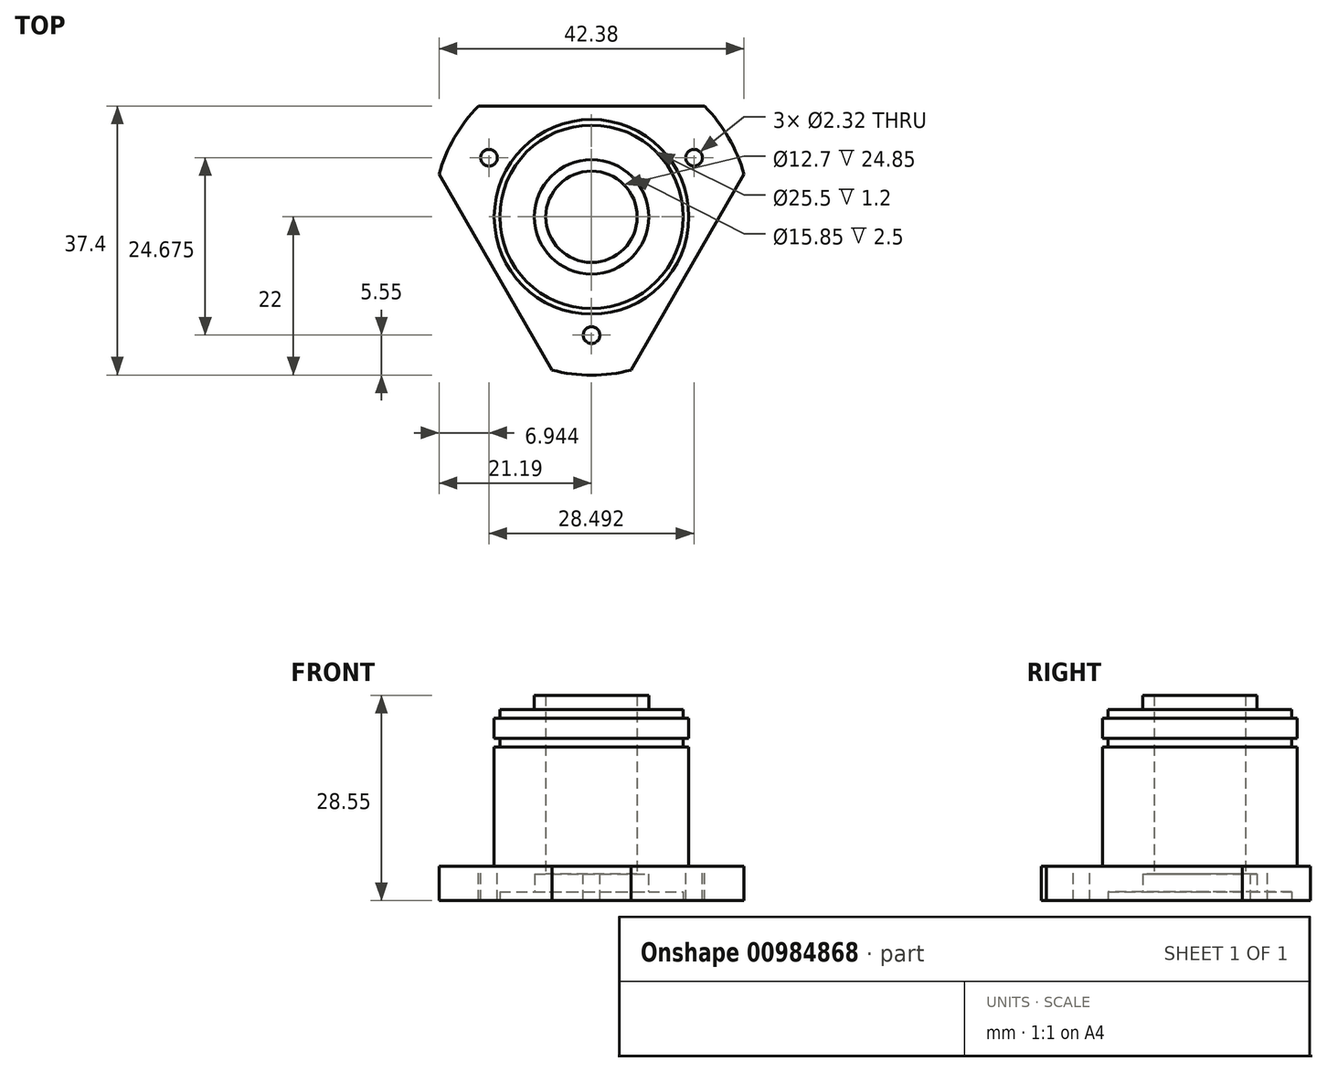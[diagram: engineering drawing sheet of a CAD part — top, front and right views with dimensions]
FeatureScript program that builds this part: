
annotation { "Feature Type Name" : "Feature", "Feature Type Description" : "" }
export const myFeature = defineFeature(function(context is Context, id is Id, definition is map)
    precondition{}
    {
        {
            var Q0;
            Q0=qCreatedBy(makeId("Top.planeOp"),FACE);
            var sketch = newSketch(context, id + "F0", { "sketchPlane" : qUnion([Q0])});
            skCircle(sketch, "E0", {"center": v(0, 0) * mm, "radius": 13.53 * mm});
            skCircle(sketch, "E1", {"center": v(0, 0) * mm, "radius": 6.35 * mm});
            skSolve(sketch);
        }
        {
            var Q0;
            Q0=makeQuery(id+"F0.imprint","IMPRINT",FACE,{"disambiguationData":[TD([[makeQuery(id+"F0.imprint","IMPRINT",EDGE,{"derivedFrom":sQuery(id+"F0.wireOp",EDGE,"E0")}),1.0]])]});
            extrude(context, id + "F1", {"entities" : qUnion([Q0]), "depth" : 23.8 * mm, "offsetDistance" : 25 * mm});
        }
        {
            var Q0;
            Q0=makeQuery(id+"F1.opExtrude","CAP_FACE",FACE,{"disambiguationData":[OSD([sQuery(id+"F0.wireOp",EDGE,"E0"),sQuery(id+"F0.wireOp",EDGE,"E1")])],"isStart":false});
            var sketch = newSketch(context, id + "F2", { "sketchPlane" : qUnion([Q0])});
            skCircle(sketch, "E2", {"center": v(0, 0) * mm, "radius": 13.53 * mm});
            skCircle(sketch, "E3", {"center": v(0, 0) * mm, "radius": 7.95 * mm});
            skSolve(sketch);
        }
        {
            var Q0;
            Q0=makeQuery(id+"F2.imprint","IMPRINT",FACE,{"disambiguationData":[TD([[makeQuery(id+"F2.imprint","IMPRINT",EDGE,{"derivedFrom":sQuery(id+"F2.wireOp",EDGE,"E2")}),1.0]])]});
            extrude(context, id + "F3", {"entities" : qUnion([Q0]), "operationType" : NewBodyOperationType.REMOVE, "oppositeDirection" : true, "depth" : 2 * mm, "offsetDistance" : 25 * mm});
        }
        {
            var Q0;
            Q0=makeQuery(id+"F3.boolean.opBoolean","COPY",FACE,{"derivedFrom":makeQuery(id+"F3.opExtrude","CAP_FACE",FACE,{"disambiguationData":[OSD([sQuery(id+"F2.wireOp",EDGE,"E2"),sQuery(id+"F2.wireOp",EDGE,"E3")])],"isStart":false})});
            var sketch = newSketch(context, id + "F4", { "sketchPlane" : qUnion([Q0])});
            skCircle(sketch, "E4", {"center": v(0, 0) * mm, "radius": 12.75 * mm});
            skCircle(sketch, "E5", {"center": v(0, 0) * mm, "radius": 13.53 * mm});
            skSolve(sketch);
        }
        {
            var Q0;
            Q0=makeQuery(id+"F4.imprint","IMPRINT",FACE,{"disambiguationData":[TD([[makeQuery(id+"F4.imprint","IMPRINT",EDGE,{"derivedFrom":sQuery(id+"F4.wireOp",EDGE,"E4")}),-1.0]])]});
            extrude(context, id + "F5", {"entities" : qUnion([Q0]), "operationType" : NewBodyOperationType.REMOVE, "oppositeDirection" : true, "depth" : 1.2 * mm, "offsetDistance" : 25 * mm});
        }
        {
            var Q0;
            Q0=makeQuery(id+"F1.opExtrude","CAP_FACE",FACE,{"disambiguationData":[OSD([sQuery(id+"F0.wireOp",EDGE,"E0"),sQuery(id+"F0.wireOp",EDGE,"E1")])],"isStart":true});
            var sketch = newSketch(context, id + "F6", { "sketchPlane" : qUnion([Q0])});
            skCircle(sketch, "E6", {"center": v(0, 0) * mm, "radius": 22 * mm});
            skCircle(sketch, "E7", {"center": v(0, 16.45) * mm, "radius": 1.16 * mm});
            skCircle(sketch, "E8.1.1", {"center": v(-14.25, -8.22) * mm, "radius": 1.16 * mm});
            skCircle(sketch, "E8.2.1", {"center": v(14.25, -8.23) * mm, "radius": 1.16 * mm});
            skLineSegment(sketch, "E9", {"start": v(-15.71, -15.4) * mm, "end": v(15.71, -15.4) * mm});
            skPoint(sketch, "E10", {"position": v(0, -15.4) * mm});
            skPoint(sketch, "E11.orphan", {"position": v(-16.5, -15.4) * mm});
            skPoint(sketch, "E12.orphan", {"position": v(16.5, -15.4) * mm});
            skLineSegment(sketch, "E13.1.0", {"start": v(21.2, -5.9) * mm, "end": v(5.48, 21.3) * mm});
            skLineSegment(sketch, "E13.2.0", {"start": v(-5.48, 21.3) * mm, "end": v(-21.2, -5.9) * mm});
            skSolve(sketch);
        }
        {
            var Q0;
            Q0=makeQuery(id+"F6.imprint","IMPRINT",FACE,{"disambiguationData":[TD([[makeQuery(id+"F6.imprint","IMPRINT",EDGE,{"derivedFrom":sQuery(id+"F6.wireOp",EDGE,"E7")}),-1.0]])]});
            var Q1;
            Q1=makeQuery(id+"F6.imprint","IMPRINT",FACE,{"disambiguationData":[TD([[makeQuery(id+"F6.imprint","IMPRINT",EDGE,{"derivedFrom":makeQuery(id+"F1.opExtrude","CAP_EDGE",EDGE,{"disambiguationData":[OSD([sQuery(id+"F0.wireOp",EDGE,"E0")])],"isStart":true})}),-1.0]])]});
            extrude(context, id + "F7", {"entities" : qUnion([Q0, Q1]), "operationType" : NewBodyOperationType.ADD, "depth" : 4.75 * mm, "offsetDistance" : 25 * mm});
        }
        {
            var Q0;
            Q0=makeQuery(id+"F7.opExtrude","CAP_FACE",FACE,{"disambiguationData":[OSD([sQuery(id+"F0.wireOp",EDGE,"E1"),sQuery(id+"F6.wireOp",EDGE,"E7"),sQuery(id+"F6.wireOp",EDGE,"E8.1.1"),sQuery(id+"F6.wireOp",EDGE,"E6"),sQuery(id+"F6.wireOp",EDGE,"E8.2.1"),sQuery(id+"F6.wireOp",EDGE,"E9"),sQuery(id+"F6.wireOp",EDGE,"E13.1.0"),sQuery(id+"F6.wireOp",EDGE,"E13.2.0")])],"isStart":false});
            var sketch = newSketch(context, id + "F8", { "sketchPlane" : qUnion([Q0])});
            skCircle(sketch, "E14", {"center": v(0, 0) * mm, "radius": 12.75 * mm});
            skSolve(sketch);
        }
        {
            var Q0;
            Q0=makeQuery(id+"F8.imprint","IMPRINT",FACE,{"disambiguationData":[TD([[makeQuery(id+"F8.imprint","IMPRINT",EDGE,{"derivedFrom":sQuery(id+"F8.wireOp",EDGE,"E14")}),1.0]])]});
            extrude(context, id + "F9", {"entities" : qUnion([Q0]), "operationType" : NewBodyOperationType.REMOVE, "oppositeDirection" : true, "depth" : 1.2 * mm, "offsetDistance" : 25 * mm});
        }
        {
            var Q0;
            Q0=makeQuery(id+"F9.boolean.opBoolean","COPY",FACE,{"derivedFrom":makeQuery(id+"F9.opExtrude","CAP_FACE",FACE,{"disambiguationData":[OSD([sQuery(id+"F0.wireOp",EDGE,"E1"),sQuery(id+"F8.wireOp",EDGE,"E14")])],"isStart":false})});
            var sketch = newSketch(context, id + "F10", { "sketchPlane" : qUnion([Q0])});
            skCircle(sketch, "E15", {"center": v(0, 0) * mm, "radius": 7.92 * mm});
            skSolve(sketch);
        }
        {
            var Q0;
            Q0=makeQuery(id+"F10.imprint","IMPRINT",FACE,{"disambiguationData":[TD([[makeQuery(id+"F10.imprint","IMPRINT",EDGE,{"derivedFrom":sQuery(id+"F10.wireOp",EDGE,"E15")}),1.0]])]});
            extrude(context, id + "F11", {"entities" : qUnion([Q0]), "operationType" : NewBodyOperationType.REMOVE, "oppositeDirection" : true, "depth" : 2.5 * mm, "offsetDistance" : 25 * mm});
        }
        {
            var Q0;
            Q0=makeQuery(id+"F3.boolean.opBoolean","COPY",FACE,{"derivedFrom":makeQuery(id+"F3.opExtrude","CAP_FACE",FACE,{"disambiguationData":[OSD([sQuery(id+"F2.wireOp",EDGE,"E2"),sQuery(id+"F2.wireOp",EDGE,"E3")])],"isStart":false})});
            cPlane(context, id + "F12", {"entities" : qUnion([Q0]), "cplaneType" : CPlaneType.OFFSET, "offset" : 4 * mm, "oppositeDirection" : true, "width" : 150 * mm, "height" : 150 * mm});
        }
        {
            var Q0;
            Q0=qCreatedBy(id+"F12.planeOp",FACE);
            var sketch = newSketch(context, id + "F13", { "sketchPlane" : qUnion([Q0])});
            skCircle(sketch, "E16", {"center": v(0, 0) * mm, "radius": 13.53 * mm});
            skCircle(sketch, "E17", {"center": v(0, 0) * mm, "radius": 12.75 * mm});
            skSolve(sketch);
        }
        {
            var Q0;
            Q0 = qSketchRegion(id + "F13", true);
            extrude(context, id + "F14", {"entities" : qUnion([Q0]), "operationType" : NewBodyOperationType.REMOVE, "oppositeDirection" : true, "depth" : 1.2 * mm, "offsetDistance" : 25 * mm});
        }
    });
